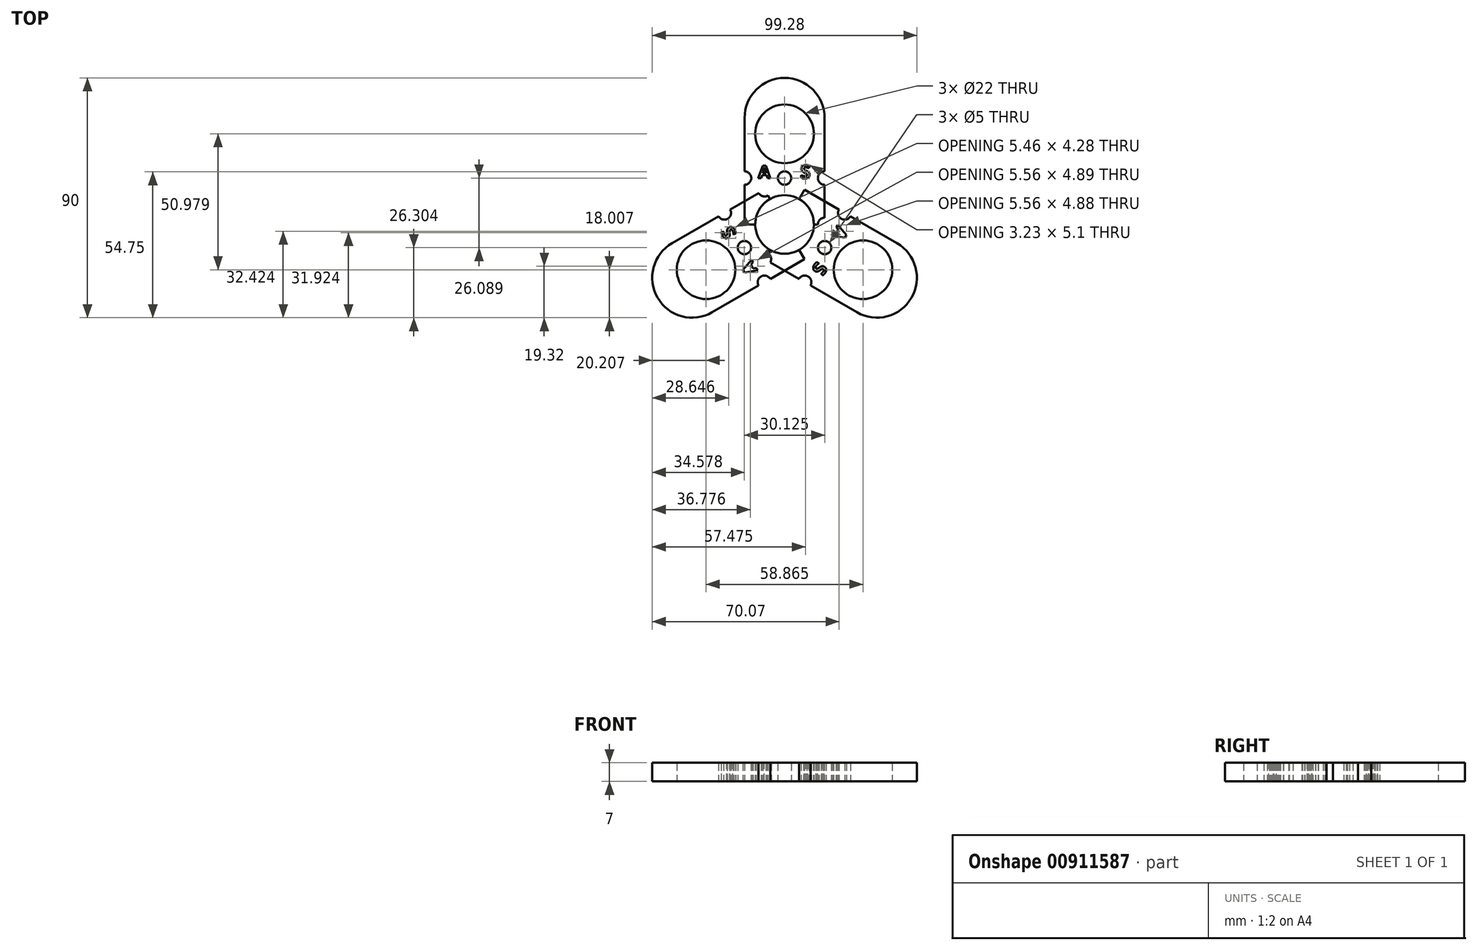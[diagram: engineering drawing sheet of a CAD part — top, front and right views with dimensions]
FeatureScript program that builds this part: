
annotation { "Feature Type Name" : "Feature", "Feature Type Description" : "" }
export const myFeature = defineFeature(function(context is Context, id is Id, definition is map)
    precondition{}
    {
        {
            var Q0;
            Q0=qCreatedBy(makeId("Top.planeOp"),FACE);
            var sketch = newSketch(context, id + "F0", { "sketchPlane" : qUnion([Q0])});
            skCircle(sketch, "E0", {"center": v(0, 0) * mm, "radius": 11 * mm});
            skLineSegment(sketch, "E1.bottom", {"start": v(0, 0) * mm, "end": v(15, 0) * mm});
            skLineSegment(sketch, "E1.right", {"start": v(15, 0) * mm, "end": v(15, 40) * mm});
            skLineSegment(sketch, "E2.bottom", {"start": v(0, 0) * mm, "end": v(-15, 0) * mm});
            skLineSegment(sketch, "E2.right", {"start": v(-15, 0) * mm, "end": v(-15, 40) * mm});
            skCircle(sketch, "E3", {"center": v(0, 33.99) * mm, "radius": 11 * mm});
            skArc(sketch, "E4", {"start": v(-15, 40) * mm, "mid": v(0, 55) * mm, "end": v(15, 40) * mm});
            skCircle(sketch, "E5", {"center": v(0, 17.4) * mm, "radius": 2.5 * mm});
            skCircle(sketch, "E6", {"center": v(15, 0) * mm, "radius": 2.5 * mm});
            skCircle(sketch, "E7", {"center": v(15, 17.4) * mm, "radius": 2.5 * mm});
            skCircle(sketch, "E8", {"center": v(-15, 17.4) * mm, "radius": 2.5 * mm});
            skText(sketch, "E9", { "text": "A\n", "fontName": "OpenSans-Bold.ttf"});
            skText(sketch, "E10", { "text": "S\n", "fontName": "OpenSans-Bold.ttf"});
            const initialGuessF0  = {"E9": [-0.00985, 0.01733, 1, 0, 0.00477], "E10": [0.0059, 0.01727, 1, 0, 0.005]};
            skSetInitialGuess(sketch, initialGuessF0);
            skSolve(sketch);
        }
        {
            var Q0;
            Q0=makeQuery(id+"F0.imprint","IMPRINT",FACE,{"disambiguationData":[TD([[makeQuery(id+"F0.imprint","IMPRINT",EDGE,{"derivedFrom":sQuery(id+"F0.wireOp",EDGE,"E9.sketch_text.stroke-8")}),1.0]])]});
            var Q1;
            Q1=makeQuery(id+"F0.imprint","IMPRINT",FACE,{"disambiguationData":[TD([[makeQuery(id+"F0.imprint","IMPRINT",EDGE,{"derivedFrom":sQuery(id+"F0.wireOp",EDGE,"E3")}),-1.0]])]});
            extrude(context, id + "F1", {"entities" : qUnion([Q0, Q1]), "depth" : 7 * mm, "offsetDistance" : 25 * mm});
        }
        {
            var Q0;
            Q0=qCreatedBy(makeId("Right.planeOp"),FACE);
            var sketch = newSketch(context, id + "F2", { "sketchPlane" : qUnion([Q0])});
            skLineSegment(sketch, "E11", {"start": v(0, 0) * mm, "end": v(0, -40.01) * mm});
            skSolve(sketch);
        }
        {
            var Q0;
            Q0=makeQuery(id+"F1.opExtrude","SWEPT_BODY",BODY,{"disambiguationData":[OSD([sQuery(id+"F0.wireOp",EDGE,"E0"),sQuery(id+"F0.wireOp",EDGE,"E1.bottom"),sQuery(id+"F0.wireOp",EDGE,"E1.top"),sQuery(id+"F0.wireOp",EDGE,"E1.right"),sQuery(id+"F0.wireOp",EDGE,"E2.bottom"),sQuery(id+"F0.wireOp",EDGE,"E2.top"),sQuery(id+"F0.wireOp",EDGE,"E2.right"),sQuery(id+"F0.wireOp",EDGE,"E3")])]});
            var Q1;
            Q1=sQuery(id+"F2.wireOp",EDGE,"E11");
            transform(context, id + "F3", {"entities" : qUnion([Q0]), "transformType" : TransformType.ROTATION, "transformAxis" : qUnion([Q1]), "angle" : 120 * degree, "makeCopy" : true});
        }
        {
            var Q0;
            Q0=makeQuery(id+"F3.opPattern","COPY",BODY,{"derivedFrom":makeQuery(id+"F1.opExtrude","SWEPT_BODY",BODY,{"disambiguationData":[OSD([sQuery(id+"F0.wireOp",EDGE,"E0"),sQuery(id+"F0.wireOp",EDGE,"E1.bottom"),sQuery(id+"F0.wireOp",EDGE,"E1.top"),sQuery(id+"F0.wireOp",EDGE,"E1.right"),sQuery(id+"F0.wireOp",EDGE,"E2.bottom"),sQuery(id+"F0.wireOp",EDGE,"E2.top"),sQuery(id+"F0.wireOp",EDGE,"E2.right"),sQuery(id+"F0.wireOp",EDGE,"E3")])]}),"instanceName":"1"});
            var Q1;
            Q1=sQuery(id+"F2.wireOp",EDGE,"E11");
            transform(context, id + "F4", {"entities" : qUnion([Q0]), "transformType" : TransformType.ROTATION, "transformAxis" : qUnion([Q1]), "angle" : 120 * degree, "makeCopy" : true});
        }
    });
